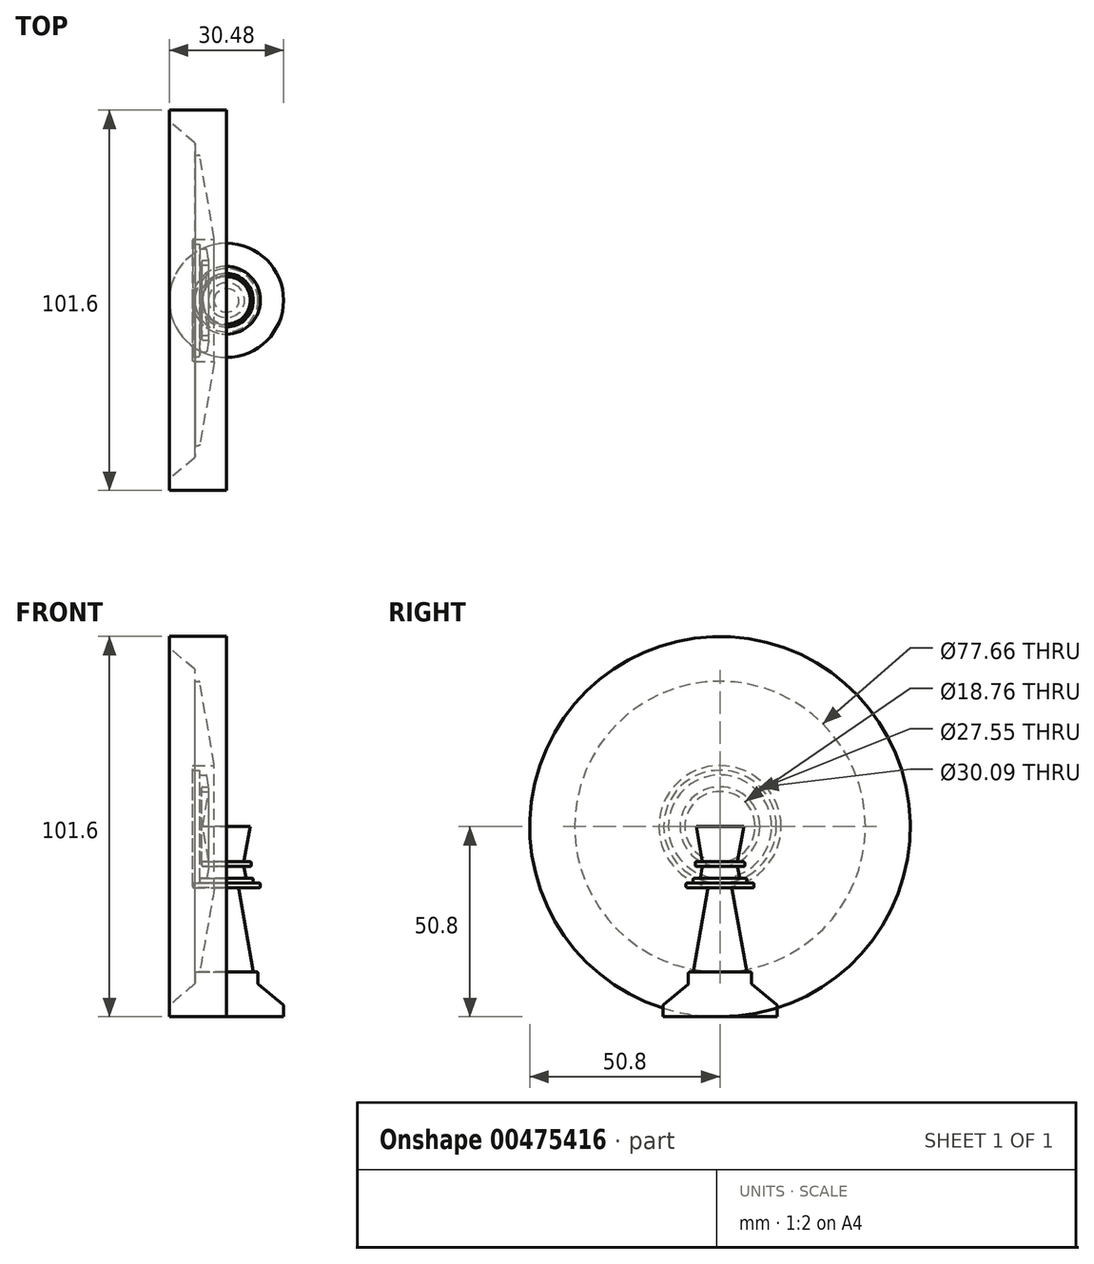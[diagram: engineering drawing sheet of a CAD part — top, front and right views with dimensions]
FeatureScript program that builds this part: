
annotation { "Feature Type Name" : "Feature", "Feature Type Description" : "" }
export const myFeature = defineFeature(function(context is Context, id is Id, definition is map)
    precondition{}
    {
        {
            var Q0;
            Q0=qCreatedBy(makeId("Front.planeOp"),FACE);
            var sketch = newSketch(context, id + "F0", { "sketchPlane" : qUnion([Q0])});
            skLineSegment(sketch, "E0.bottom", {"start": v(0, 0) * mm, "end": v(-15.24, 0) * mm});
            skLineSegment(sketch, "E0.top", {"start": v(0, 50.8) * mm, "end": v(-6.35, 50.8) * mm});
            skLineSegment(sketch, "E0.left", {"start": v(0, 0) * mm, "end": v(0, 50.8) * mm});
            skLineSegment(sketch, "E1", {"start": v(-15.24, 0) * mm, "end": v(-15.24, 2.93) * mm});
            skLineSegment(sketch, "E2", {"start": v(-15.13, 3.18) * mm, "end": v(-8.54, 8.7) * mm});
            skLineSegment(sketch, "E3", {"start": v(-8.43, 8.94) * mm, "end": v(-8.43, 11.65) * mm});
            skLineSegment(sketch, "E4", {"start": v(-8.11, 11.97) * mm, "end": v(-7.43, 11.97) * mm});
            skLineSegment(sketch, "E5", {"start": v(-7.11, 12.23) * mm, "end": v(-3.26, 34.11) * mm});
            skLineSegment(sketch, "E6", {"start": v(-3.57, 34.48) * mm, "end": v(-8.74, 34.48) * mm});
            skLineSegment(sketch, "E7", {"start": v(-9.06, 34.8) * mm, "end": v(-9.06, 35.44) * mm});
            skLineSegment(sketch, "E8", {"start": v(-8.74, 35.75) * mm, "end": v(-7.47, 35.75) * mm});
            skLineSegment(sketch, "E9", {"start": v(-7.15, 36.07) * mm, "end": v(-7.15, 36.7) * mm});
            skLineSegment(sketch, "E10", {"start": v(-6.83, 37.02) * mm, "end": v(-5.51, 37.02) * mm});
            skLineSegment(sketch, "E11", {"start": v(-5.2, 37.29) * mm, "end": v(-4.76, 39.78) * mm});
            skLineSegment(sketch, "E12", {"start": v(-5.07, 40.15) * mm, "end": v(-6.28, 40.15) * mm});
            skLineSegment(sketch, "E13", {"start": v(-6.6, 40.47) * mm, "end": v(-6.6, 41.1) * mm});
            skLineSegment(sketch, "E14", {"start": v(-6.28, 41.42) * mm, "end": v(-5.07, 41.42) * mm});
            skLineSegment(sketch, "E15", {"start": v(-4.76, 41.8) * mm, "end": v(-6.35, 50.8) * mm});
            skPoint(sketch, "E16.visualSharp", {"position": v(-15.24, 3.08) * mm});
            skArc(sketch, "E16.filletArc", {"start": v(-15.13, 3.18) * mm, "mid": v(-15.21, 3.07) * mm, "end": v(-15.24, 2.93) * mm});
            skPoint(sketch, "E17.visualSharp", {"position": v(-8.43, 8.8) * mm});
            skArc(sketch, "E17.filletArc", {"start": v(-8.54, 8.7) * mm, "mid": v(-8.46, 8.8) * mm, "end": v(-8.43, 8.94) * mm});
            skPoint(sketch, "E18.visualSharp", {"position": v(-3.2, 34.48) * mm});
            skArc(sketch, "E18.filletArc", {"start": v(-3.26, 34.11) * mm, "mid": v(-3.33, 34.37) * mm, "end": v(-3.57, 34.48) * mm});
            skPoint(sketch, "E19.visualSharp", {"position": v(-8.43, 11.97) * mm});
            skArc(sketch, "E19.filletArc", {"start": v(-8.11, 11.97) * mm, "mid": v(-8.34, 11.88) * mm, "end": v(-8.43, 11.65) * mm});
            skPoint(sketch, "E20.visualSharp", {"position": v(-7.16, 11.97) * mm});
            skArc(sketch, "E20.filletArc", {"start": v(-7.43, 11.97) * mm, "mid": v(-7.22, 12.04) * mm, "end": v(-7.11, 12.23) * mm});
            skPoint(sketch, "E21.visualSharp", {"position": v(-9.06, 34.48) * mm});
            skArc(sketch, "E21.filletArc", {"start": v(-9.06, 34.8) * mm, "mid": v(-8.96, 34.58) * mm, "end": v(-8.74, 34.48) * mm});
            skPoint(sketch, "E22.visualSharp", {"position": v(-9.06, 35.75) * mm});
            skArc(sketch, "E22.filletArc", {"start": v(-8.74, 35.75) * mm, "mid": v(-8.96, 35.66) * mm, "end": v(-9.06, 35.44) * mm});
            skPoint(sketch, "E23.visualSharp", {"position": v(-7.15, 35.75) * mm});
            skArc(sketch, "E23.filletArc", {"start": v(-7.47, 35.75) * mm, "mid": v(-7.25, 35.85) * mm, "end": v(-7.15, 36.07) * mm});
            skPoint(sketch, "E24.visualSharp", {"position": v(-7.15, 37.02) * mm});
            skArc(sketch, "E24.filletArc", {"start": v(-6.83, 37.02) * mm, "mid": v(-7.06, 36.93) * mm, "end": v(-7.15, 36.7) * mm});
            skPoint(sketch, "E25.visualSharp", {"position": v(-5.25, 37.02) * mm});
            skArc(sketch, "E25.filletArc", {"start": v(-5.51, 37.02) * mm, "mid": v(-5.3, 37.1) * mm, "end": v(-5.2, 37.29) * mm});
            skPoint(sketch, "E26.visualSharp", {"position": v(-4.7, 40.15) * mm});
            skArc(sketch, "E26.filletArc", {"start": v(-4.76, 39.78) * mm, "mid": v(-4.83, 40.04) * mm, "end": v(-5.07, 40.15) * mm});
            skPoint(sketch, "E27.visualSharp", {"position": v(-6.6, 40.15) * mm});
            skArc(sketch, "E27.filletArc", {"start": v(-6.6, 40.47) * mm, "mid": v(-6.5, 40.24) * mm, "end": v(-6.28, 40.15) * mm});
            skPoint(sketch, "E28.visualSharp", {"position": v(-6.6, 41.42) * mm});
            skArc(sketch, "E28.filletArc", {"start": v(-6.28, 41.42) * mm, "mid": v(-6.5, 41.33) * mm, "end": v(-6.6, 41.1) * mm});
            skPoint(sketch, "E29.visualSharp", {"position": v(-4.7, 41.42) * mm});
            skArc(sketch, "E29.filletArc", {"start": v(-5.07, 41.42) * mm, "mid": v(-4.83, 41.53) * mm, "end": v(-4.76, 41.8) * mm});
            skLineSegment(sketch, "E30", {"start": v(0, 0) * mm, "end": v(0, 63.7) * mm, "construction": true});
            skSolve(sketch);
        }
        {
            var Q0;
            Q0=makeQuery(id+"F0.imprint","IMPRINT",FACE,{"disambiguationData":[TD([[makeQuery(id+"F0.imprint","IMPRINT",EDGE,{"derivedFrom":sQuery(id+"F0.wireOp",EDGE,"E0.bottom")}),-1.0]])]});
            var Q1;
            Q1=sQuery(id+"F0.wireOp",EDGE,"E0.top");
            revolve(context, id + "F1", {"entities" : qUnion([Q0]), "axis" : qUnion([Q1]), "revolveType" : RevolveType.FULL});
        }
        {
            var Q0;
            Q0=makeQuery(id+"F0.imprint","IMPRINT",FACE,{"disambiguationData":[TD([[makeQuery(id+"F0.imprint","IMPRINT",EDGE,{"derivedFrom":sQuery(id+"F0.wireOp",EDGE,"E0.bottom")}),-1.0]])]});
            var Q1;
            Q1=sQuery(id+"F0.wireOp",EDGE,"E0.left");
            revolve(context, id + "F2", {"entities" : qUnion([Q0]), "axis" : qUnion([Q1]), "revolveType" : RevolveType.FULL});
        }
    });
